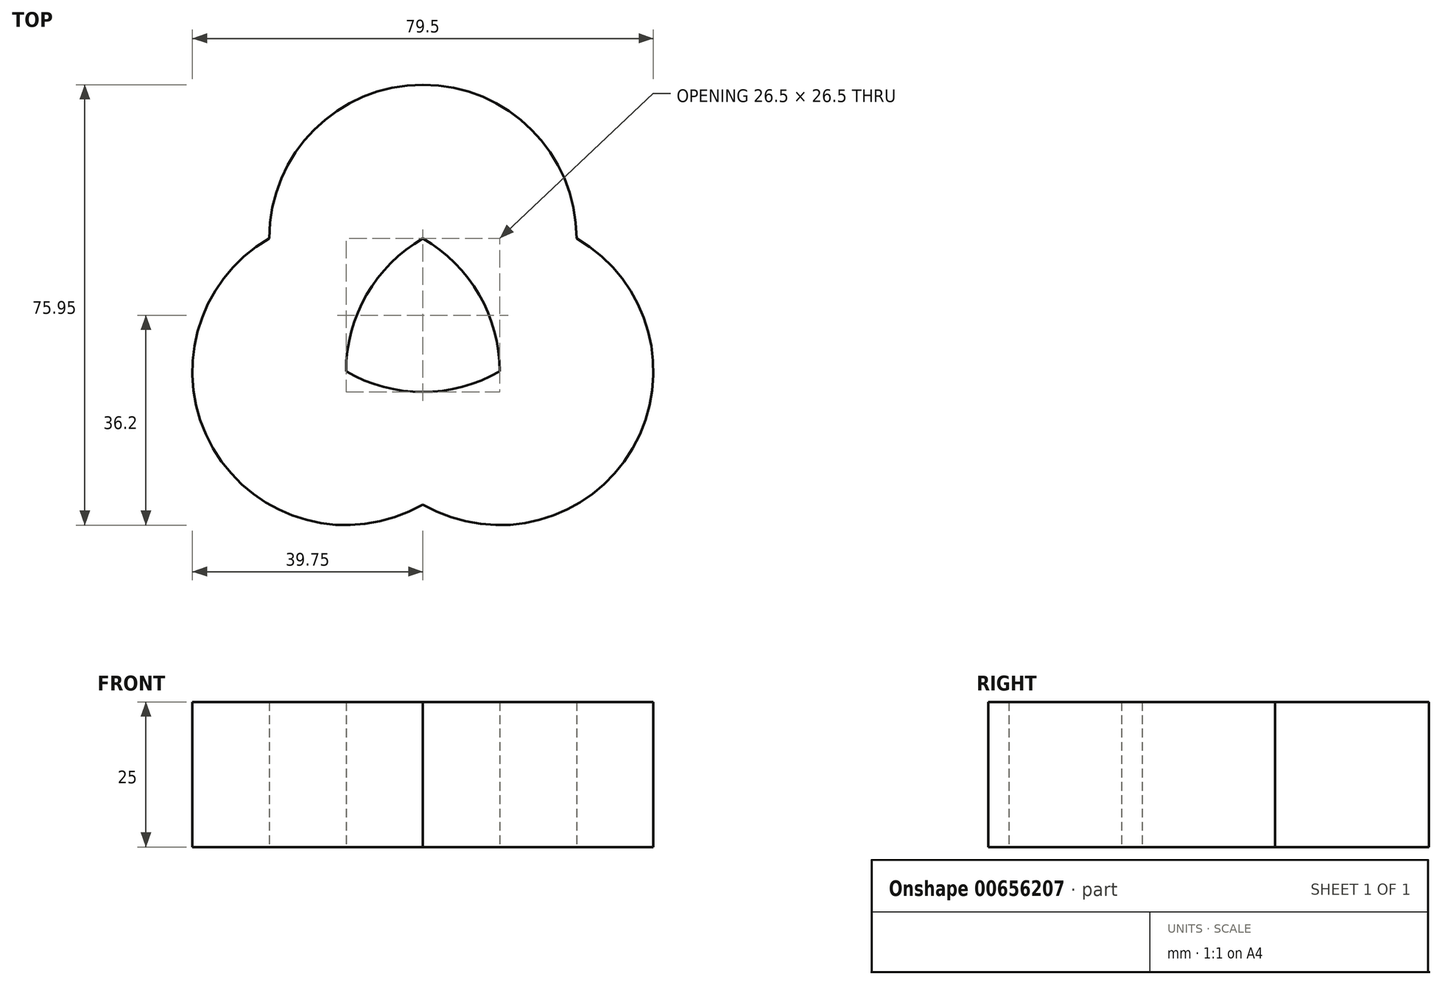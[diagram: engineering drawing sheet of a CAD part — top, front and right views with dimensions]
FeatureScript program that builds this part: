
annotation { "Feature Type Name" : "Feature", "Feature Type Description" : "" }
export const myFeature = defineFeature(function(context is Context, id is Id, definition is map)
    precondition{}
    {
        {
            var Q0;
            Q0=qCreatedBy(makeId("Top.planeOp"),FACE);
            var sketch = newSketch(context, id + "F0", { "sketchPlane" : qUnion([Q0])});
            skCircle(sketch, "E0", {"center": v(0, 0) * mm, "radius": 26.5 * mm});
            skCircle(sketch, "E1", {"center": v(-26.5, 0) * mm, "radius": 26.5 * mm});
            skCircle(sketch, "E2", {"center": v(-13.25, 22.95) * mm, "radius": 26.5 * mm});
            skSolve(sketch);
        }
        {
            var Q0;
            {var subQ0=sQuery(id+"F0.wireOp",EDGE,"E2");var subQ1=sQuery(id+"F0.wireOp",EDGE,"E0");var subQ2=makeQuery(id+"F0.imprint","INTERSECT",VERTEX,{"disambiguationData":[OD(0.0)],"derivedFrom":[subQ1,subQ0]});Q0=makeQuery(id+"F0.imprint","IMPRINT",FACE,{"disambiguationData":[TD([[makeQuery(id+"F0.imprint","IMPRINT",EDGE,{"disambiguationData":[TD([[subQ2,-1.0]])],"derivedFrom":subQ1}),-1.0]])]});}
            var Q1;
            {var subQ0=sQuery(id+"F0.wireOp",EDGE,"E2");var subQ1=sQuery(id+"F0.wireOp",EDGE,"E0");var subQ2=makeQuery(id+"F0.imprint","INTERSECT",VERTEX,{"disambiguationData":[OD(0.0)],"derivedFrom":[subQ1,subQ0]});Q1=makeQuery(id+"F0.imprint","IMPRINT",FACE,{"disambiguationData":[TD([[makeQuery(id+"F0.imprint","IMPRINT",EDGE,{"disambiguationData":[TD([[subQ2,1.0]])],"derivedFrom":subQ1}),1.0]])]});}
            var Q2;
            {var subQ0=sQuery(id+"F0.wireOp",EDGE,"E1");var subQ1=sQuery(id+"F0.wireOp",EDGE,"E0");var subQ2=makeQuery(id+"F0.imprint","INTERSECT",VERTEX,{"disambiguationData":[OD(0.0)],"derivedFrom":[subQ1,subQ0]});Q2=makeQuery(id+"F0.imprint","IMPRINT",FACE,{"disambiguationData":[TD([[makeQuery(id+"F0.imprint","IMPRINT",EDGE,{"disambiguationData":[TD([[subQ2,1.0]])],"derivedFrom":subQ1}),-1.0]])]});}
            var Q3;
            {var subQ0=sQuery(id+"F0.wireOp",EDGE,"E1");var subQ1=sQuery(id+"F0.wireOp",EDGE,"E0");var subQ2=makeQuery(id+"F0.imprint","INTERSECT",VERTEX,{"disambiguationData":[OD(1.0)],"derivedFrom":[subQ1,subQ0]});Q3=makeQuery(id+"F0.imprint","IMPRINT",FACE,{"disambiguationData":[TD([[makeQuery(id+"F0.imprint","IMPRINT",EDGE,{"disambiguationData":[TD([[subQ2,-1.0]])],"derivedFrom":subQ1}),-1.0]])]});}
            var Q4;
            {var subQ0=sQuery(id+"F0.wireOp",EDGE,"E1");var subQ1=sQuery(id+"F0.wireOp",EDGE,"E0");var subQ2=makeQuery(id+"F0.imprint","INTERSECT",VERTEX,{"disambiguationData":[OD(0.0)],"derivedFrom":[subQ1,subQ0]});Q4=makeQuery(id+"F0.imprint","IMPRINT",FACE,{"disambiguationData":[TD([[makeQuery(id+"F0.imprint","IMPRINT",EDGE,{"disambiguationData":[TD([[subQ2,1.0]])],"derivedFrom":subQ1}),1.0]])]});}
            var Q5;
            {var subQ0=sQuery(id+"F0.wireOp",EDGE,"E2");var subQ1=sQuery(id+"F0.wireOp",EDGE,"E0");var subQ2=makeQuery(id+"F0.imprint","INTERSECT",VERTEX,{"disambiguationData":[OD(0.0)],"derivedFrom":[subQ1,subQ0]});Q5=makeQuery(id+"F0.imprint","IMPRINT",FACE,{"disambiguationData":[TD([[makeQuery(id+"F0.imprint","IMPRINT",EDGE,{"disambiguationData":[TD([[subQ2,-1.0]])],"derivedFrom":subQ1}),1.0]])]});}
            extrude(context, id + "F1", {"entities" : qUnion([Q0, Q1, Q2, Q3, Q4, Q5]), "depth" : 25 * mm, "offsetDistance" : 25 * mm});
        }
    });
